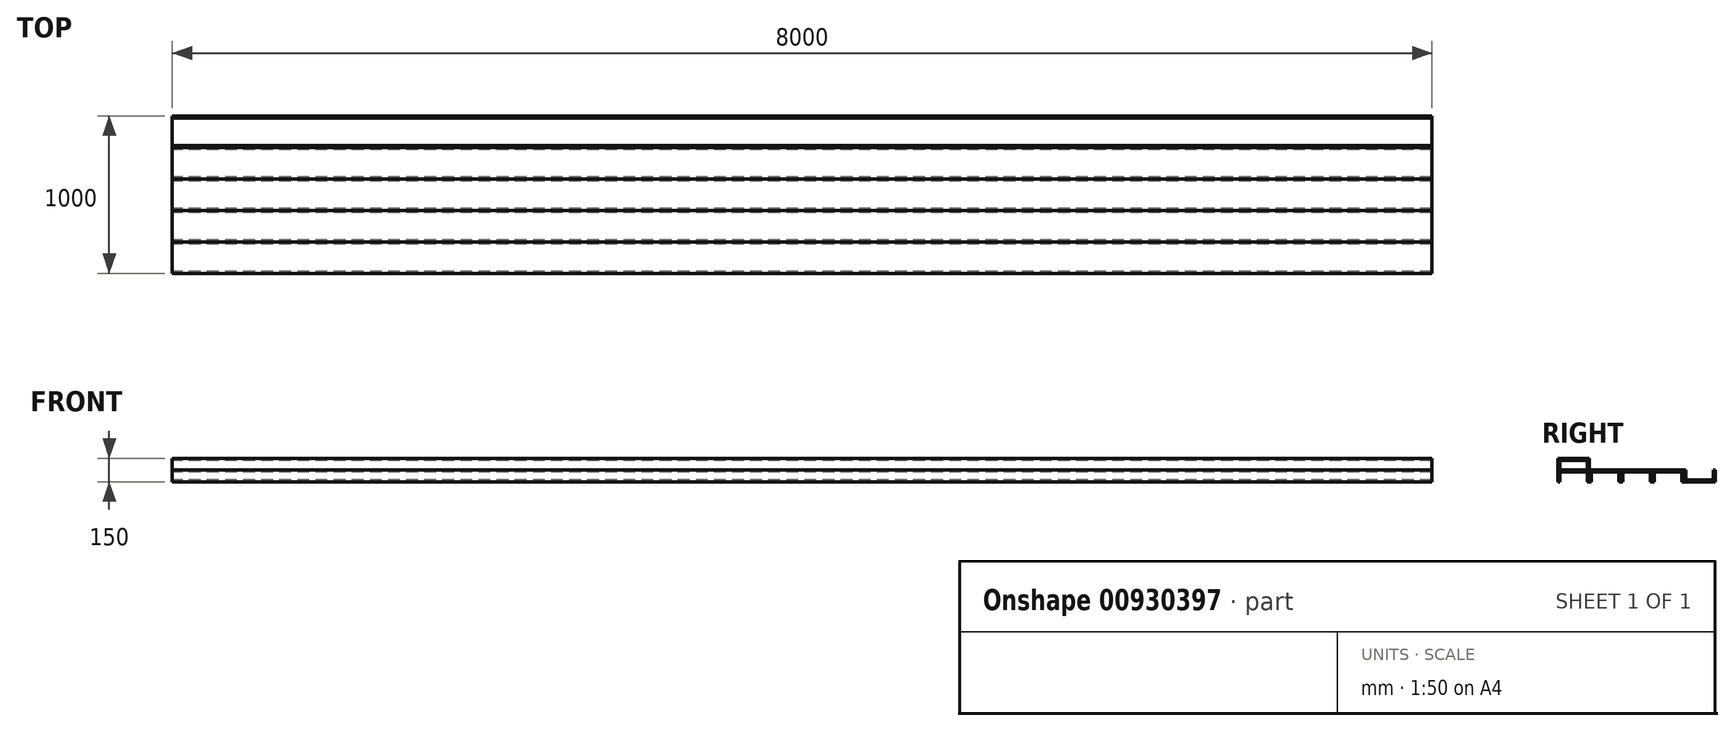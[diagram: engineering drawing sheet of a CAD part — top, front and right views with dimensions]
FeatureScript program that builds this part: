
annotation { "Feature Type Name" : "Feature", "Feature Type Description" : "" }
export const myFeature = defineFeature(function(context is Context, id is Id, definition is map)
    precondition{}
    {
        {
            var Q0;
            Q0=qCreatedBy(makeId("Right.planeOp"),FACE);
            var sketch = newSketch(context, id + "F0", { "sketchPlane" : qUnion([Q0])});
            skLineSegment(sketch, "E0", {"start": v(0, 0) * mm, "end": v(0, -75) * mm});
            skLineSegment(sketch, "E1", {"start": v(0, -75) * mm, "end": v(-200, -75) * mm});
            skLineSegment(sketch, "E2", {"start": v(-200, -75) * mm, "end": v(-200, 0) * mm});
            skLineSegment(sketch, "E3", {"start": v(-200, 0) * mm, "end": v(-400, 0) * mm});
            skLineSegment(sketch, "E4", {"start": v(-400, 0) * mm, "end": v(-400, -75) * mm});
            skLineSegment(sketch, "E5", {"start": v(-400, 0) * mm, "end": v(-600, 0) * mm});
            skLineSegment(sketch, "E6", {"start": v(-600, 0) * mm, "end": v(-600, -75) * mm});
            skLineSegment(sketch, "E7", {"start": v(-600, 0) * mm, "end": v(-800, 0) * mm});
            skLineSegment(sketch, "E8", {"start": v(-800, 0) * mm, "end": v(-800, -75) * mm});
            skLineSegment(sketch, "E9", {"start": v(-800, 0) * mm, "end": v(-1000, 0) * mm});
            skLineSegment(sketch, "E10", {"start": v(-1000, 0) * mm, "end": v(-1000, -75) * mm});
            skLineSegment(sketch, "E11", {"start": v(-1000, -75) * mm, "end": v(-988, -75) * mm});
            skLineSegment(sketch, "E12", {"start": v(-988, -75) * mm, "end": v(-988, -12) * mm});
            skLineSegment(sketch, "E13", {"start": v(-988, -12) * mm, "end": v(-812, -12) * mm});
            skLineSegment(sketch, "E14", {"start": v(-812, -12) * mm, "end": v(-812, -75) * mm});
            skLineSegment(sketch, "E15", {"start": v(-812, -75) * mm, "end": v(-800, -75) * mm});
            skLineSegment(sketch, "E16", {"start": v(-800, -75) * mm, "end": v(-788, -75) * mm});
            skLineSegment(sketch, "E17", {"start": v(-788, -75) * mm, "end": v(-788, -12) * mm});
            skLineSegment(sketch, "E18", {"start": v(-788, -12) * mm, "end": v(-612, -12) * mm});
            skLineSegment(sketch, "E19", {"start": v(-612, -12) * mm, "end": v(-612, -75) * mm});
            skLineSegment(sketch, "E20", {"start": v(-612, -75) * mm, "end": v(-600, -75) * mm});
            skLineSegment(sketch, "E21", {"start": v(-600, -75) * mm, "end": v(-588, -75) * mm});
            skLineSegment(sketch, "E22", {"start": v(-588, -75) * mm, "end": v(-588, -12) * mm});
            skLineSegment(sketch, "E23", {"start": v(-588, -12) * mm, "end": v(-412, -12) * mm});
            skLineSegment(sketch, "E24", {"start": v(-412, -12) * mm, "end": v(-412, -75) * mm});
            skLineSegment(sketch, "E25", {"start": v(-412, -75) * mm, "end": v(-400, -75) * mm});
            skLineSegment(sketch, "E26", {"start": v(-400, -75) * mm, "end": v(-388, -75) * mm});
            skLineSegment(sketch, "E27", {"start": v(-388, -75) * mm, "end": v(-388, -12) * mm});
            skLineSegment(sketch, "E28", {"start": v(-388, -12) * mm, "end": v(-212, -12) * mm});
            skLineSegment(sketch, "E29", {"start": v(-212, -12) * mm, "end": v(-212, -75) * mm});
            skLineSegment(sketch, "E30", {"start": v(-212, -75) * mm, "end": v(-200, -75) * mm});
            skLineSegment(sketch, "E31", {"start": v(-200, 0) * mm, "end": v(-188, 0) * mm});
            skLineSegment(sketch, "E32", {"start": v(-188, 0) * mm, "end": v(-188, -63) * mm});
            skLineSegment(sketch, "E33", {"start": v(-188, -63) * mm, "end": v(-12, -63) * mm});
            skLineSegment(sketch, "E34", {"start": v(-12, -63) * mm, "end": v(-12, 0) * mm});
            skLineSegment(sketch, "E35", {"start": v(-12, 0) * mm, "end": v(0, 0) * mm});
            skLineSegment(sketch, "E36", {"start": v(-1000, 0) * mm, "end": v(-1000, 75) * mm});
            skLineSegment(sketch, "E37", {"start": v(-1000, 75) * mm, "end": v(-800, 75) * mm});
            skLineSegment(sketch, "E38", {"start": v(-800, 75) * mm, "end": v(-800, 0) * mm});
            skLineSegment(sketch, "E39", {"start": v(-988, 0) * mm, "end": v(-988, 63) * mm});
            skLineSegment(sketch, "E40", {"start": v(-988, 63) * mm, "end": v(-812, 63) * mm});
            skLineSegment(sketch, "E41", {"start": v(-812, 63) * mm, "end": v(-812, 0) * mm});
            skSolve(sketch);
        }
        {
            var Q0;
            Q0=makeQuery(id+"F0.imprint","IMPRINT",FACE,{"disambiguationData":[TD([[makeQuery(id+"F0.imprint","IMPRINT",EDGE,{"derivedFrom":sQuery(id+"F0.wireOp",EDGE,"E0")}),-1.0]])]});
            extrude(context, id + "F1", {"entities" : qUnion([Q0]), "depth" : 8000 * mm, "offsetDistance" : 25 * mm});
        }
        {
            var Q0;
            Q0=makeQuery(id+"F0.imprint","IMPRINT",FACE,{"disambiguationData":[TD([[makeQuery(id+"F0.imprint","IMPRINT",EDGE,{"derivedFrom":sQuery(id+"F0.wireOp",EDGE,"E2")}),1.0]])]});
            extrude(context, id + "F2", {"entities" : qUnion([Q0]), "depth" : 8000 * mm, "offsetDistance" : 25 * mm});
        }
        {
            var Q0;
            Q0=makeQuery(id+"F0.imprint","IMPRINT",FACE,{"disambiguationData":[TD([[makeQuery(id+"F0.imprint","IMPRINT",EDGE,{"derivedFrom":sQuery(id+"F0.wireOp",EDGE,"E4")}),-1.0]])]});
            extrude(context, id + "F3", {"entities" : qUnion([Q0]), "depth" : 8000 * mm, "offsetDistance" : 25 * mm});
        }
        {
            var Q0;
            Q0=makeQuery(id+"F0.imprint","IMPRINT",FACE,{"disambiguationData":[TD([[makeQuery(id+"F0.imprint","IMPRINT",EDGE,{"derivedFrom":sQuery(id+"F0.wireOp",EDGE,"E6")}),-1.0]])]});
            extrude(context, id + "F4", {"entities" : qUnion([Q0]), "depth" : 8000 * mm, "offsetDistance" : 25 * mm});
        }
        {
            var Q0;
            Q0=makeQuery(id+"F0.imprint","IMPRINT",FACE,{"disambiguationData":[TD([[makeQuery(id+"F0.imprint","IMPRINT",EDGE,{"derivedFrom":sQuery(id+"F0.wireOp",EDGE,"E8")}),-1.0]])]});
            extrude(context, id + "F5", {"entities" : qUnion([Q0]), "depth" : 8000 * mm, "offsetDistance" : 25 * mm});
        }
        {
            var Q0;
            {var subQ0=sQuery(id+"F0.wireOp",EDGE,"E36");Q0=makeQuery(id+"F0.imprint","IMPRINT",FACE,{"disambiguationData":[TD([[makeQuery(id+"F0.imprint","IMPRINT",EDGE,{"derivedFrom":subQ0}),-1.0]])]});}
            extrude(context, id + "F6", {"entities" : qUnion([Q0]), "depth" : 8000 * mm, "offsetDistance" : 25 * mm});
        }
    });
